# Revit family: ColumnCover_GRG_CastleAccess
name_source: partatom
category: Generic Models
units: mm (PartAtom-declared; Revit-internal decimal feet)

## family parameters
Always vertical = Yes
Can host rebar = No
Cut with Voids When Loaded = No
Maintain Annotation Orientation = No
Part Type = Normal
Room Calculation Point = No
Round Connector Dimension = Use Diameter
Shared = No
Work Plane-Based = Yes

## types (1)
- ColumnCover_GRG_CastleAccess
    Assembly Code = C3010300
    Column Diameter = 1' - 1"
    Construction Details = https://www.castleaccesspanels.com
    Cost = 0 $
    Default Elevation = 4' - 0"
    Diameter = 1' - 0"
    Expected Lifespan (Years) = 0
    Green Building-LEED = https://www.arcat.com
    Installation Phase = Plaster and Gypsum Board - Column Finishes
    Installation-Fabrication = https://www.castleaccesspanels.com
    Keynote = 09 27 13
    Maintenance Schedule (Months) = 0
    Manufacturer = Castle Access Panels & Forms Inc.
    Manufacturer Fax = (+1)905-760-9234
    Manufacturer Website = https://www.castleaccesspanels.com
    Material = Castle Access_Glass Reinforced Gypsum (GRG) Column Cover
    Product Data = https://www.castleaccesspanels.com
    Product Properties = https://www.castleaccesspanels.com
    Revision = R#_01-2018
    Send Message = https://www.castleaccesspanels.com
    URL = https://www.arcat.com
    Unit Height = 4' - 0"
    Warranty Duration (Years) = 3

## geometry (parser evidence)
native form markers: Sweep x1
no freeform markers — native parametric forms only
